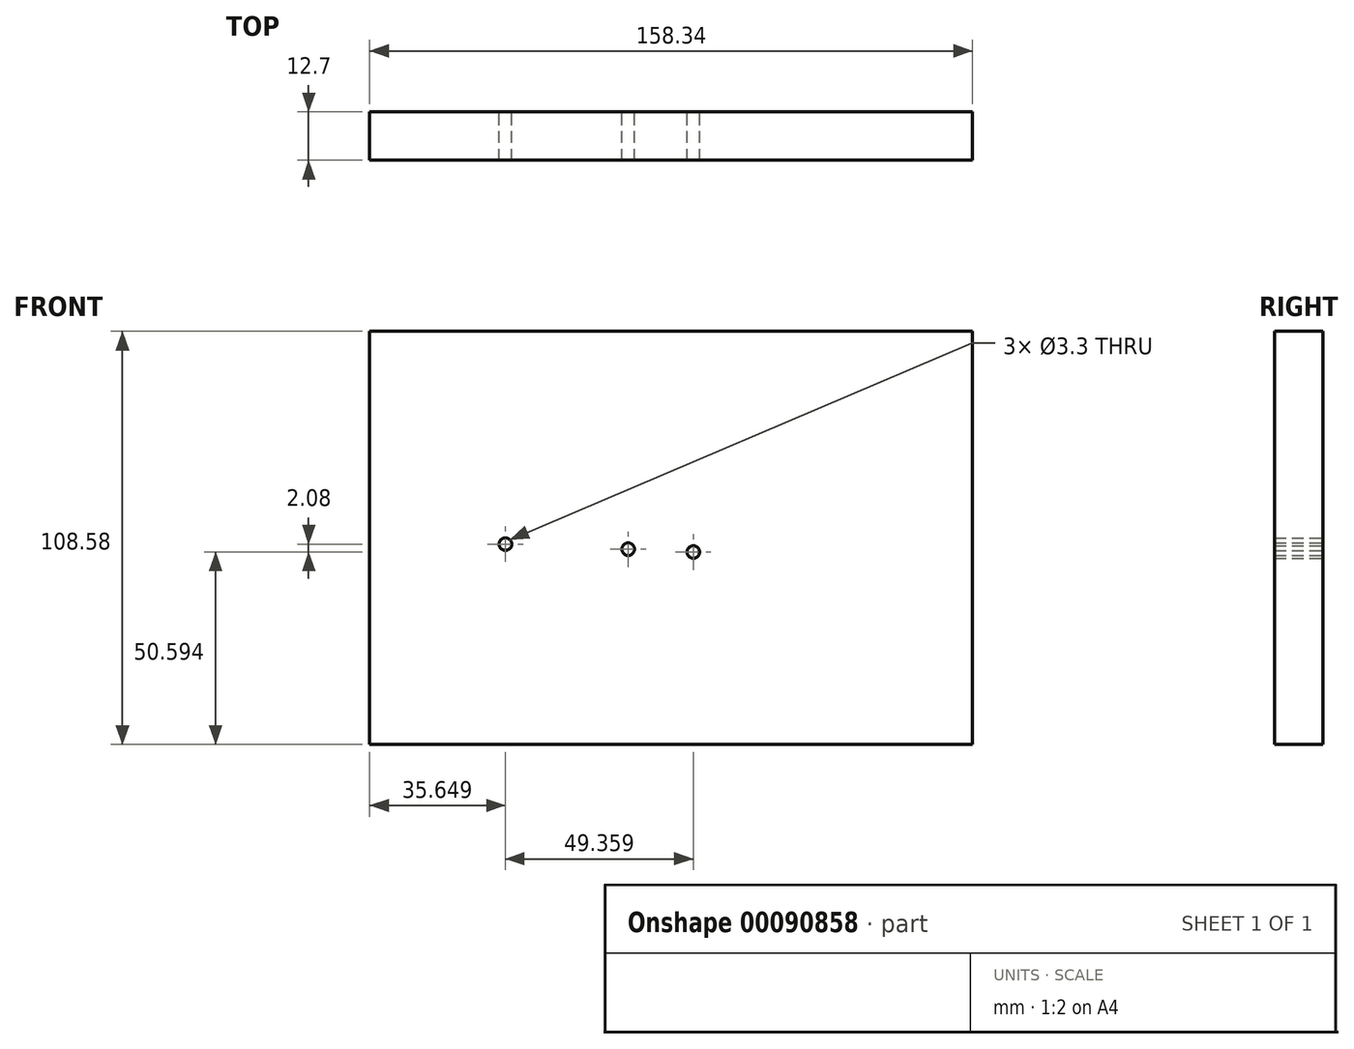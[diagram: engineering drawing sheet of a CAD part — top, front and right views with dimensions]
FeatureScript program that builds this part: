
annotation { "Feature Type Name" : "Feature", "Feature Type Description" : "" }
export const myFeature = defineFeature(function(context is Context, id is Id, definition is map)
    precondition{}
    {
        {
            var Q0;
            Q0=qCreatedBy(makeId("Front.planeOp"),FACE);
            var sketch = newSketch(context, id + "F0", { "sketchPlane" : qUnion([Q0])});
            skLineSegment(sketch, "E0.bottom", {"start": v(-55.74, 65.34) * mm, "end": v(102.6, 65.34) * mm});
            skLineSegment(sketch, "E0.top", {"start": v(-55.74, -43.24) * mm, "end": v(102.6, -43.24) * mm});
            skLineSegment(sketch, "E0.left", {"start": v(-55.74, 65.34) * mm, "end": v(-55.74, -43.24) * mm});
            skLineSegment(sketch, "E0.right", {"start": v(102.6, 65.34) * mm, "end": v(102.6, -43.24) * mm});
            skCircle(sketch, "E1", {"center": v(-20.1, 9.43) * mm, "radius": 1.65 * mm});
            skCircle(sketch, "E2", {"center": v(12.17, 8.1) * mm, "radius": 1.65 * mm});
            skCircle(sketch, "E3", {"center": v(29.27, 7.35) * mm, "radius": 1.65 * mm});
            skLineSegment(sketch, "E4", {"start": v(-20.1, 9.43) * mm, "end": v(12.17, 8.1) * mm});
            skLineSegment(sketch, "E5", {"start": v(12.17, 8.1) * mm, "end": v(29.27, 7.35) * mm});
            skSolve(sketch);
        }
        {
            var Q0;
            Q0=makeQuery(id+"F0.imprint","IMPRINT",FACE,{"disambiguationData":[TD([[makeQuery(id+"F0.imprint","IMPRINT",EDGE,{"derivedFrom":sQuery(id+"F0.wireOp",EDGE,"E0.bottom")}),-1.0]])]});
            extrude(context, id + "F1", {"entities" : qUnion([Q0]), "depth" : 12.7 * mm});
        }
    });
